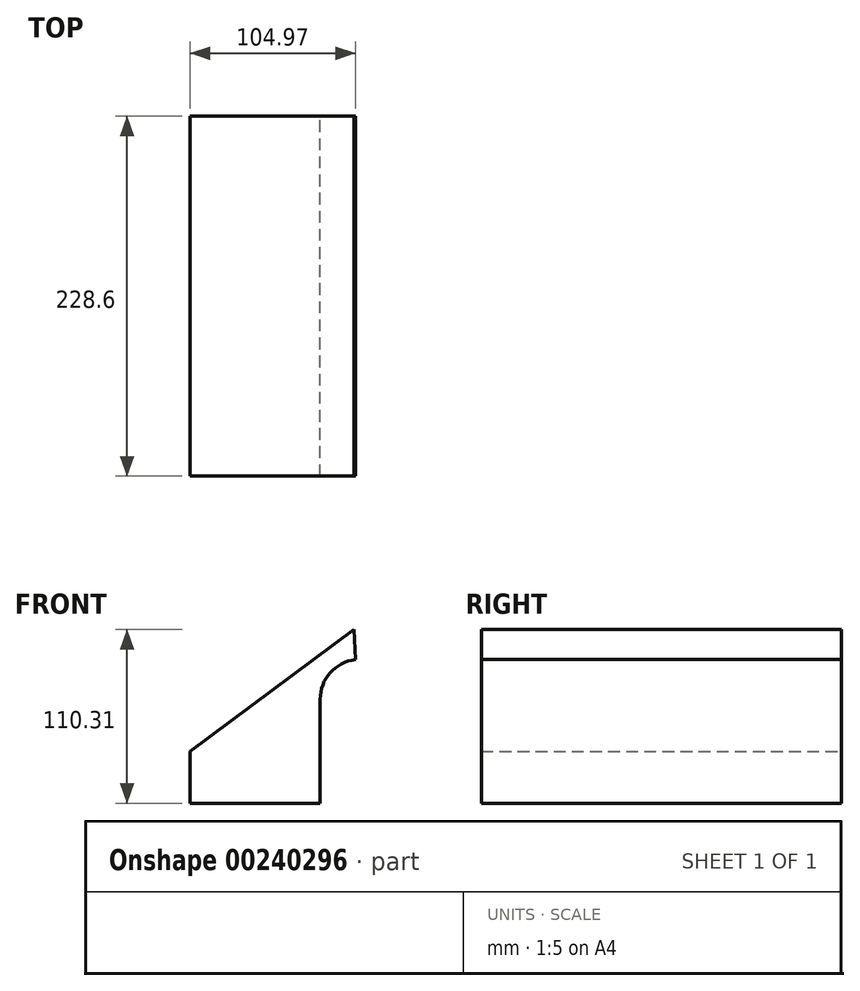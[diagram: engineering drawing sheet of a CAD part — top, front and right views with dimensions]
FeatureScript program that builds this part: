
annotation { "Feature Type Name" : "Feature", "Feature Type Description" : "" }
export const myFeature = defineFeature(function(context is Context, id is Id, definition is map)
    precondition{}
    {
        {
            var Q0;
            Q0=qCreatedBy(makeId("Front.planeOp"),FACE);
            var sketch = newSketch(context, id + "F0", { "sketchPlane" : qUnion([Q0])});
            skLineSegment(sketch, "E0.bottom", {"start": v(-41.28, 16.5) * mm, "end": v(41.27, 16.51) * mm});
            skLineSegment(sketch, "E0.top", {"start": v(-41.28, -16.51) * mm, "end": v(41.28, -16.51) * mm});
            skLineSegment(sketch, "E0.left", {"start": v(-41.28, 16.5) * mm, "end": v(-41.27, -16.51) * mm});
            skLineSegment(sketch, "E0.right", {"start": v(41.27, 16.51) * mm, "end": v(41.28, -16.5) * mm});
            skPoint(sketch, "E0.middle", {"position": v(0, 0) * mm});
            skLineSegment(sketch, "E1.bottom", {"start": v(63.7, -26.85) * mm, "end": v(162.76, -26.85) * mm});
            skLineSegment(sketch, "E1.top", {"start": v(63.7, 176.35) * mm, "end": v(162.76, 176.35) * mm});
            skLineSegment(sketch, "E1.left", {"start": v(63.7, -26.85) * mm, "end": v(63.7, 176.35) * mm});
            skLineSegment(sketch, "E1.right", {"start": v(162.76, -26.85) * mm, "end": v(162.76, 176.35) * mm});
            skPoint(sketch, "E1.middle", {"position": v(113.23, 74.75) * mm});
            skLineSegment(sketch, "E2", {"start": v(41.27, 16.51) * mm, "end": v(41.27, 49.53) * mm});
            skArc(sketch, "E3", {"start": v(41.27, 49.53) * mm, "mid": v(47.7, 66.4) * mm, "end": v(63.7, 74.75) * mm});
            skLineSegment(sketch, "E4", {"start": v(63.7, 74.75) * mm, "end": v(117.29, 74.75) * mm});
            skLineSegment(sketch, "E5.0", {"start": v(62.73, 93.8) * mm, "end": v(117.29, 93.8) * mm});
            skArc(sketch, "E5.1", {"start": v(22.22, 49.53) * mm, "mid": v(33.88, 79.53) * mm, "end": v(62.73, 93.8) * mm});
            skLineSegment(sketch, "E5.2", {"start": v(22.22, 16.51) * mm, "end": v(22.22, 49.53) * mm});
            skLineSegment(sketch, "E6", {"start": v(62.73, 93.8) * mm, "end": v(63.7, 74.75) * mm});
            skFitSpline(sketch, "E7", {"points": [v(-41.28, 16.5) * mm, v(62.73, 93.8) * mm], "startDerivative": vector(104, 77.3) * mm, "endDerivative": vector(104, 77.3) * mm});
            skSolve(sketch);
        }
        {
            var Q0;
            Q0=makeQuery(id+"F0.imprint","IMPRINT",FACE,{"disambiguationData":[TD([[makeQuery(id+"F0.imprint","IMPRINT",EDGE,{"derivedFrom":sQuery(id+"F0.wireOp",EDGE,"E0.top")}),1.0]])]});
            var Q1;
            {var subQ4=sQuery(id+"F0.wireOp",EDGE,"E2");Q1=makeQuery(id+"F0.imprint","IMPRINT",FACE,{"disambiguationData":[TD([[makeQuery(id+"F0.imprint","IMPRINT",EDGE,{"derivedFrom":subQ4}),1.0]])]});}
            var Q2;
            {var subQ0=sQuery(id+"F0.wireOp",EDGE,"E7");var subQ1=sQuery(id+"F0.wireOp",EDGE,"E5.1");var subQ3=makeQuery(id+"F0.imprint","INTERSECT",VERTEX,{"derivedFrom":[subQ1,subQ0]});Q2=makeQuery(id+"F0.imprint","IMPRINT",FACE,{"disambiguationData":[TD([[makeQuery(id+"F0.imprint","IMPRINT",EDGE,{"disambiguationData":[TD([[subQ3,-1.0]])],"derivedFrom":subQ1}),-1.0]])]});}
            extrude(context, id + "F1", {"entities" : qUnion([Q0, Q1, Q2]), "endBound" : BoundingType.SYMMETRIC, "depth" : 228.6 * mm});
        }
    });
